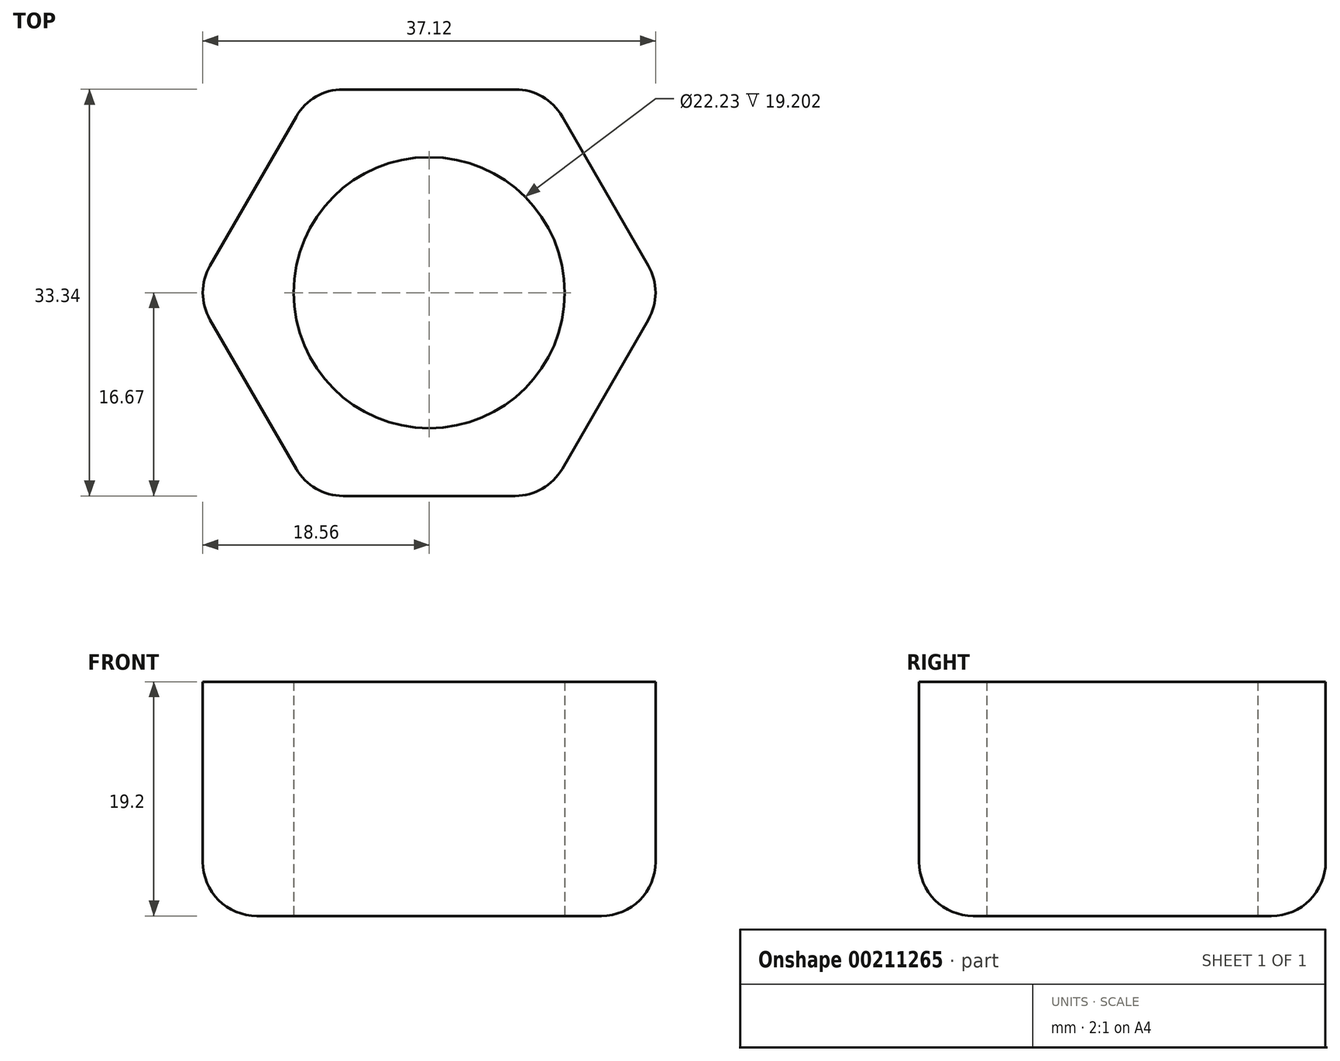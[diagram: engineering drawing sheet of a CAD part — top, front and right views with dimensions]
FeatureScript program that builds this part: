
annotation { "Feature Type Name" : "Feature", "Feature Type Description" : "" }
export const myFeature = defineFeature(function(context is Context, id is Id, definition is map)
    precondition{}
    {
        {
            var Q0;
            Q0=qCreatedBy(makeId("Top.planeOp"),FACE);
            var sketch = newSketch(context, id + "F0", { "sketchPlane" : qUnion([Q0])});
            skCircle(sketch, "E0.cCircle", {"center": v(0, 0) * mm, "radius": 11.9 * mm, "construction": true});
            skLineSegment(sketch, "E0.0", {"start": v(-6.87, 11.9) * mm, "end": v(6.87, 11.9) * mm});
            skLineSegment(sketch, "E0.1", {"start": v(6.87, 11.9) * mm, "end": v(13.75, 0) * mm});
            skLineSegment(sketch, "E0.2", {"start": v(13.75, 0) * mm, "end": v(6.87, -11.9) * mm});
            skLineSegment(sketch, "E0.3", {"start": v(6.87, -11.9) * mm, "end": v(-6.87, -11.9) * mm});
            skLineSegment(sketch, "E0.4", {"start": v(-6.87, -11.9) * mm, "end": v(-13.75, 0) * mm});
            skLineSegment(sketch, "E0.5", {"start": v(-13.75, 0) * mm, "end": v(-6.87, 11.9) * mm});
            skPoint(sketch, "E0.0.midPoint", {"position": v(0, 11.9) * mm});
            skCircle(sketch, "E1", {"center": v(0, 0) * mm, "radius": 7.94 * mm});
            skSolve(sketch);
        }
        {
            var Q0;
            Q0 = qSketchRegion(id + "F0", true);
            extrude(context, id + "F1", {"entities" : qUnion([Q0]), "depth" : 13.72 * mm});
        }
        {
            var Q0;
            Q0=makeQuery(id+"F1.opExtrude","SWEPT_EDGE",EDGE,{"disambiguationData":[OSD([sQuery(id+"F0.wireOp",EDGE,"E0.4"),sQuery(id+"F0.wireOp",EDGE,"E0.5")])]});
            var Q1;
            Q1=makeQuery(id+"F1.opExtrude","CAP_EDGE",EDGE,{"disambiguationData":[OSD([sQuery(id+"F0.wireOp",EDGE,"E0.2")])],"isStart":true});
            var Q2;
            Q2=makeQuery(id+"F1.opExtrude","SWEPT_EDGE",EDGE,{"disambiguationData":[OSD([sQuery(id+"F0.wireOp",EDGE,"E0.1"),sQuery(id+"F0.wireOp",EDGE,"E0.2")])]});
            var Q3;
            Q3=makeQuery(id+"F1.opExtrude","SWEPT_EDGE",EDGE,{"disambiguationData":[OSD([sQuery(id+"F0.wireOp",EDGE,"E0.2"),sQuery(id+"F0.wireOp",EDGE,"E0.3")])]});
            var Q4;
            Q4=makeQuery(id+"F1.opExtrude","SWEPT_EDGE",EDGE,{"disambiguationData":[OSD([sQuery(id+"F0.wireOp",EDGE,"E0.3"),sQuery(id+"F0.wireOp",EDGE,"E0.4")])]});
            var Q5;
            Q5=makeQuery(id+"F1.opExtrude","SWEPT_EDGE",EDGE,{"disambiguationData":[OSD([sQuery(id+"F0.wireOp",EDGE,"E0.0"),sQuery(id+"F0.wireOp",EDGE,"E0.1")])]});
            var Q6;
            Q6=makeQuery(id+"F1.opExtrude","SWEPT_EDGE",EDGE,{"disambiguationData":[OSD([sQuery(id+"F0.wireOp",EDGE,"E0.0"),sQuery(id+"F0.wireOp",EDGE,"E0.5")])]});
            var Q7;
            Q7=makeQuery(id+"F1.opExtrude","CAP_EDGE",EDGE,{"disambiguationData":[OSD([sQuery(id+"F0.wireOp",EDGE,"E0.3")])],"isStart":true});
            var Q8;
            Q8=makeQuery(id+"F1.opExtrude","CAP_EDGE",EDGE,{"disambiguationData":[OSD([sQuery(id+"F0.wireOp",EDGE,"E0.4")])],"isStart":true});
            var Q9;
            Q9=makeQuery(id+"F1.opExtrude","CAP_EDGE",EDGE,{"disambiguationData":[OSD([sQuery(id+"F0.wireOp",EDGE,"E0.5")])],"isStart":true});
            var Q10;
            Q10=makeQuery(id+"F1.opExtrude","CAP_EDGE",EDGE,{"disambiguationData":[OSD([sQuery(id+"F0.wireOp",EDGE,"E0.0")])],"isStart":true});
            var Q11;
            Q11=makeQuery(id+"F1.opExtrude","CAP_EDGE",EDGE,{"disambiguationData":[OSD([sQuery(id+"F0.wireOp",EDGE,"E0.1")])],"isStart":true});
            fillet(context, id + "F2", {"entities" : qUnion([Q0, Q1, Q2, Q3, Q4, Q5, Q6, Q7, Q8, Q9, Q10, Q11]), "radius" : 3.17 * mm, "tangentPropagation" : true, "allowEdgeOverflow" : false});
        }
        {
            var Q0;
            Q0=makeQuery(id+"F1.opExtrude","SWEPT_BODY",BODY,{"disambiguationData":[OSD([sQuery(id+"F0.wireOp",EDGE,"E0.0"),sQuery(id+"F0.wireOp",EDGE,"E0.1"),sQuery(id+"F0.wireOp",EDGE,"E0.2"),sQuery(id+"F0.wireOp",EDGE,"E0.3"),sQuery(id+"F0.wireOp",EDGE,"E0.4"),sQuery(id+"F0.wireOp",EDGE,"E0.5"),sQuery(id+"F0.wireOp",EDGE,"E1")])]});
            var Q1;
            Q1=qCreatedBy(makeId("Origin.pointOp"),VERTEX);
            transform(context, id + "F3", {"entities" : qUnion([Q0]), "transformType" : TransformType.SCALE_UNIFORMLY, "scale" : 1.4, "scalePoint" : qUnion([Q1]), "makeCopy" : false});
        }
    });
